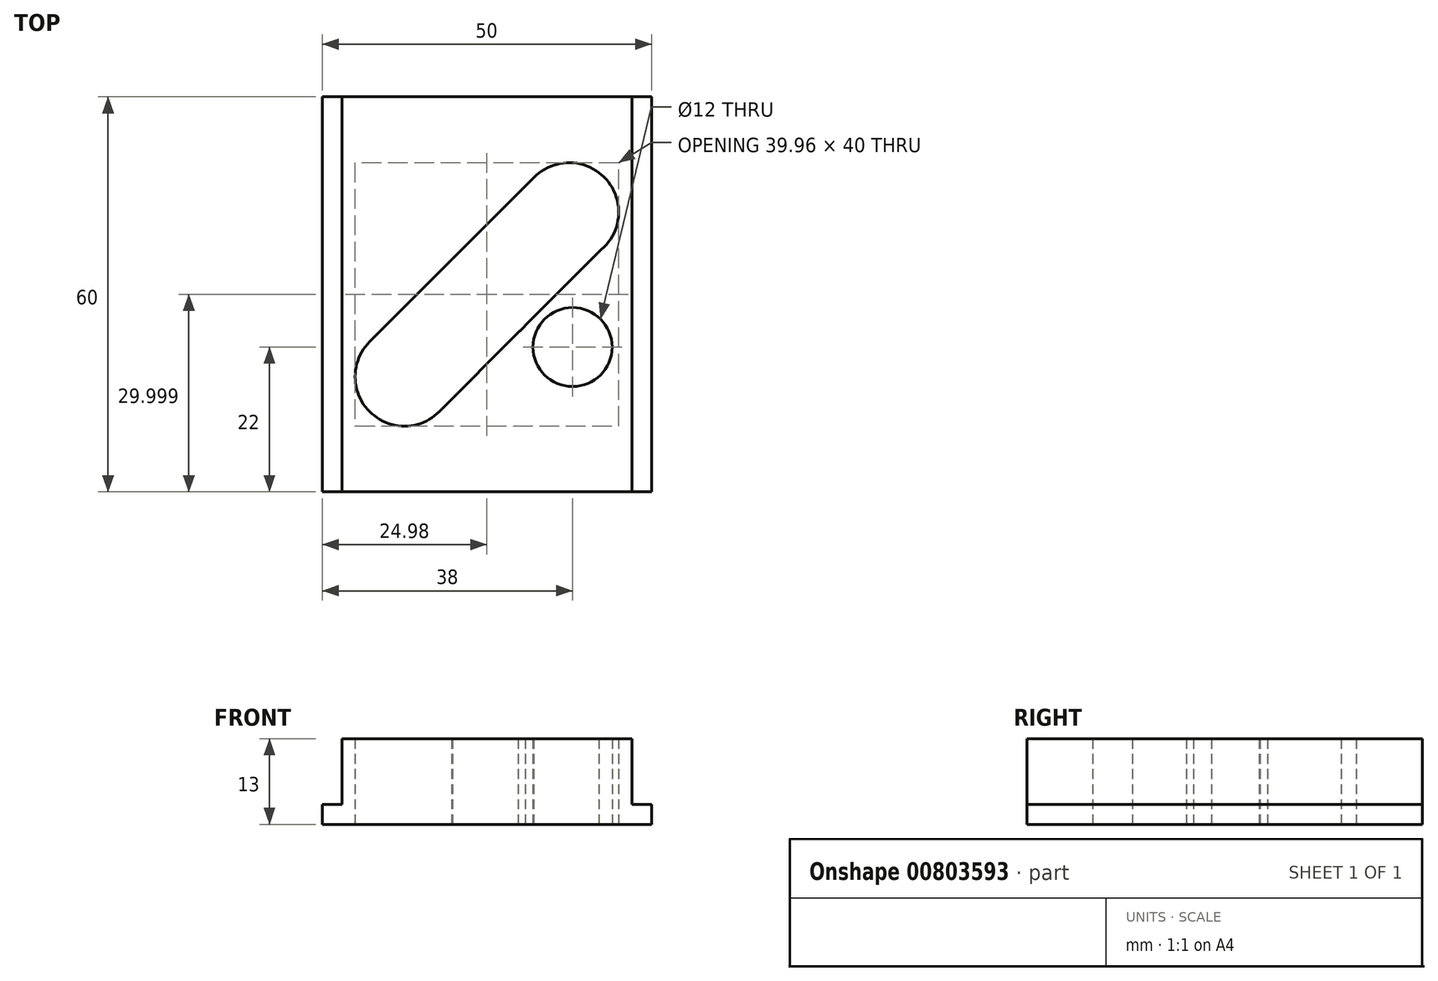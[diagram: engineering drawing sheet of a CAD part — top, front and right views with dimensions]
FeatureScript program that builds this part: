
annotation { "Feature Type Name" : "Feature", "Feature Type Description" : "" }
export const myFeature = defineFeature(function(context is Context, id is Id, definition is map)
    precondition{}
    {
        {
            var Q0;
            Q0=qCreatedBy(makeId("Top.planeOp"),FACE);
            var sketch = newSketch(context, id + "F0", { "sketchPlane" : qUnion([Q0])});
            skLineSegment(sketch, "E0.bottom", {"start": v(-25, 30) * mm, "end": v(25, 30) * mm});
            skLineSegment(sketch, "E0.top", {"start": v(-25, -30) * mm, "end": v(25, -30) * mm});
            skLineSegment(sketch, "E0.left", {"start": v(-25, 30) * mm, "end": v(-25, -30) * mm});
            skLineSegment(sketch, "E0.right", {"start": v(25, 30) * mm, "end": v(25, -30) * mm});
            skLineSegment(sketch, "E1", {"start": v(-25, 20) * mm, "end": v(25, 20) * mm, "construction": true});
            skLineSegment(sketch, "E2", {"start": v(-25, -20) * mm, "end": v(25, -20) * mm, "construction": true});
            skArc(sketch, "E3", {"start": v(4.75, -5.8) * mm, "mid": v(5.31, -5.3) * mm, "end": v(5.82, -4.73) * mm});
            skLineSegment(sketch, "E4", {"start": v(20, 30) * mm, "end": v(20, -30) * mm, "construction": true});
            skLineSegment(sketch, "E5", {"start": v(-20, 30) * mm, "end": v(-20, -30) * mm, "construction": true});
            skPoint(sketch, "E6", {"position": v(12.5, 12.5) * mm});
            skPoint(sketch, "E7", {"position": v(-12.5, -12.5) * mm});
            skArc(sketch, "E8", {"start": v(-17.8, -7.2) * mm, "mid": v(-17.8, -17.8) * mm, "end": v(-7.19, -17.8) * mm});
            skArc(sketch, "E9", {"start": v(17, 6.5) * mm, "mid": v(18.12, 17.46) * mm, "end": v(7.1, 17.71) * mm});
            skLineSegment(sketch, "E10", {"start": v(18.52, 8.02) * mm, "end": v(-7.19, -17.8) * mm});
            skLineSegment(sketch, "E11", {"start": v(7.29, 17.9) * mm, "end": v(-17.8, -7.2) * mm});
            skArc(sketch, "E12.trimOffspring", {"start": v(-5.24, 5.37) * mm, "mid": v(-5.3, 5.3) * mm, "end": v(-5.37, 5.24) * mm});
            skCircle(sketch, "E13", {"center": v(13, -8) * mm, "radius": 6 * mm});
            skSolve(sketch);
        }
        {
            var Q0;
            Q0 = qSketchRegion(id + "F0", true);
            extrude(context, id + "F1", {"entities" : qUnion([Q0]), "depth" : 13 * mm, "offsetDistance" : 25 * mm});
        }
        {
            var Q0;
            Q0=makeQuery(id+"F1.opExtrude","CAP_FACE",FACE,{"disambiguationData":[OSD([sQuery(id+"F0.wireOp",EDGE,"E0.bottom"),sQuery(id+"F0.wireOp",EDGE,"E0.top"),sQuery(id+"F0.wireOp",EDGE,"E0.left"),sQuery(id+"F0.wireOp",EDGE,"E0.right"),sQuery(id+"F0.wireOp",EDGE,"E3"),sQuery(id+"F0.wireOp",EDGE,"E8"),sQuery(id+"F0.wireOp",EDGE,"E9"),sQuery(id+"F0.wireOp",EDGE,"E10"),sQuery(id+"F0.wireOp",EDGE,"E11"),sQuery(id+"F0.wireOp",EDGE,"E12.trimOffspring"),sQuery(id+"F0.wireOp",EDGE,"E13")])],"isStart":false});
            var sketch = newSketch(context, id + "F2", { "sketchPlane" : qUnion([Q0])});
            skLineSegment(sketch, "E14.bottom", {"start": v(-25, 30) * mm, "end": v(-22, 30) * mm});
            skLineSegment(sketch, "E14.top", {"start": v(-25, -30) * mm, "end": v(-22, -30) * mm});
            skLineSegment(sketch, "E14.left", {"start": v(-25, 30) * mm, "end": v(-25, -30) * mm});
            skLineSegment(sketch, "E14.right", {"start": v(-22, 30) * mm, "end": v(-22, -30) * mm});
            skLineSegment(sketch, "E15.bottom", {"start": v(25, 30) * mm, "end": v(22, 30) * mm});
            skLineSegment(sketch, "E15.top", {"start": v(25, -30) * mm, "end": v(22, -30) * mm});
            skLineSegment(sketch, "E15.left", {"start": v(25, 30) * mm, "end": v(25, -30) * mm});
            skLineSegment(sketch, "E15.right", {"start": v(22, 30) * mm, "end": v(22, -30) * mm});
            skSolve(sketch);
        }
        {
            var Q0;
            Q0 = qSketchRegion(id + "F2", true);
            extrude(context, id + "F3", {"entities" : qUnion([Q0]), "operationType" : NewBodyOperationType.REMOVE, "oppositeDirection" : true, "depth" : 10 * mm, "offsetDistance" : 25 * mm});
        }
    });
